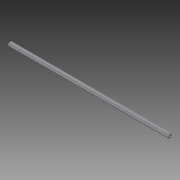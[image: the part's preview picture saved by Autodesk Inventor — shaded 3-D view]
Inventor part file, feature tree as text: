
AUTODESK INVENTOR PART (.ipt)
format: ipt  version: 2015 SP1 (Build 190203100, 203)  size: 142,336 bytes
history: native  units: in
note: dims shown in document units (in); Inventor stores cm internally (conversion verified against a paired STEP export)
features: extrude x1, sketch x1
ambient origin geometry x8: Origin, YZ Plane, XZ Plane, XY Plane, X Axis, Y Axis, Z Axis, Center Point
bodies: Solid1 (feature_tree)
feature tree (2):
  extrude  "Extrusion1"  Depth=0.5in
  sketch  "Sketch1"  dims[d0=0.5in d1=0.5in d2=0.5in d3=120.0deg d4=120.0deg d5=0.25in d6=0.25in d7=0.25in d11=0.0312in d12=0.0938in d13=0.0938in d14=0.0938in d15=0.0938in d16=0.0938in d17=0.0938in d18=0.0938in d19=0.0938in d20=0.0938in d21=0.0938in d22=0.0938in d23=0.0938in d24=150.0deg d25=150.0deg d26=150.0deg d27=90.0deg d28=90.0deg d29=30.0deg d30=30.0deg d31=30.0deg d32=30.0deg d33=90.0deg d34=90.0deg d35=150.0deg d36=0.25in d37=21.5in d38=0.0in]
